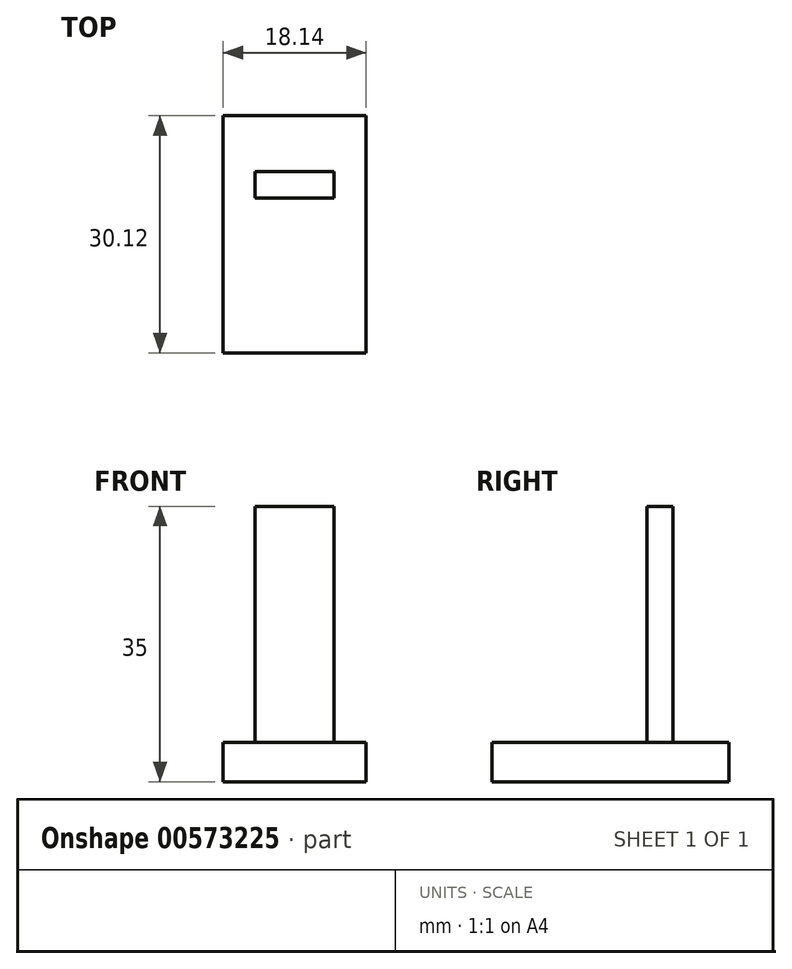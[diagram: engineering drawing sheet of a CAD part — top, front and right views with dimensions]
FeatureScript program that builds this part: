
annotation { "Feature Type Name" : "Feature", "Feature Type Description" : "" }
export const myFeature = defineFeature(function(context is Context, id is Id, definition is map)
    precondition{}
    {
        {
            var Q0;
            Q0=qCreatedBy(makeId("Top.planeOp"),FACE);
            var sketch = newSketch(context, id + "F0", { "sketchPlane" : qUnion([Q0])});
            skLineSegment(sketch, "E0.bottom", {"start": v(9.07, 15.06) * mm, "end": v(-9.07, 15.06) * mm});
            skLineSegment(sketch, "E0.top", {"start": v(9.07, -15.06) * mm, "end": v(-9.07, -15.06) * mm});
            skLineSegment(sketch, "E0.left", {"start": v(9.07, 15.06) * mm, "end": v(9.07, -15.06) * mm});
            skLineSegment(sketch, "E0.right", {"start": v(-9.07, 15.06) * mm, "end": v(-9.07, -15.06) * mm});
            skPoint(sketch, "E0.middle", {"position": v(0, 0) * mm});
            skSolve(sketch);
        }
        {
            var Q0;
            Q0=makeQuery(id+"F0.imprint","IMPRINT",FACE,{"disambiguationData":[TD([[makeQuery(id+"F0.imprint","IMPRINT",EDGE,{"derivedFrom":sQuery(id+"F0.wireOp",EDGE,"E0.bottom")}),1.0]])]});
            extrude(context, id + "F1", {"entities" : qUnion([Q0]), "depth" : 5 * mm, "offsetDistance" : 25 * mm});
        }
        {
            var Q0;
            Q0=makeQuery(id+"F1.opExtrude","CAP_FACE",FACE,{"disambiguationData":[OSD([sQuery(id+"F0.wireOp",EDGE,"E0.bottom"),sQuery(id+"F0.wireOp",EDGE,"E0.top"),sQuery(id+"F0.wireOp",EDGE,"E0.left"),sQuery(id+"F0.wireOp",EDGE,"E0.right")])],"isStart":false});
            var sketch = newSketch(context, id + "F2", { "sketchPlane" : qUnion([Q0])});
            skCircle(sketch, "E1", {"center": v(0, 12.18) * mm, "radius": 1.66 * mm});
            skLineSegment(sketch, "E2.bottom", {"start": v(5.03, 4.62) * mm, "end": v(-5.03, 4.62) * mm});
            skLineSegment(sketch, "E2.top", {"start": v(5.03, 7.96) * mm, "end": v(-5.03, 7.96) * mm});
            skLineSegment(sketch, "E2.left", {"start": v(5.03, 4.62) * mm, "end": v(5.03, 7.96) * mm});
            skLineSegment(sketch, "E2.right", {"start": v(-5.03, 4.62) * mm, "end": v(-5.03, 7.96) * mm});
            skPoint(sketch, "E2.middle", {"position": v(0, 6.3) * mm});
            skSolve(sketch);
        }
        {
            var Q0;
            Q0=makeQuery(id+"F2.imprint","IMPRINT",FACE,{"disambiguationData":[TD([[makeQuery(id+"F2.imprint","IMPRINT",EDGE,{"derivedFrom":sQuery(id+"F2.wireOp",EDGE,"E2.bottom")}),-1.0]])]});
            extrude(context, id + "F3", {"entities" : qUnion([Q0]), "operationType" : NewBodyOperationType.ADD, "depth" : 30 * mm, "offsetDistance" : 25 * mm});
        }
    });
